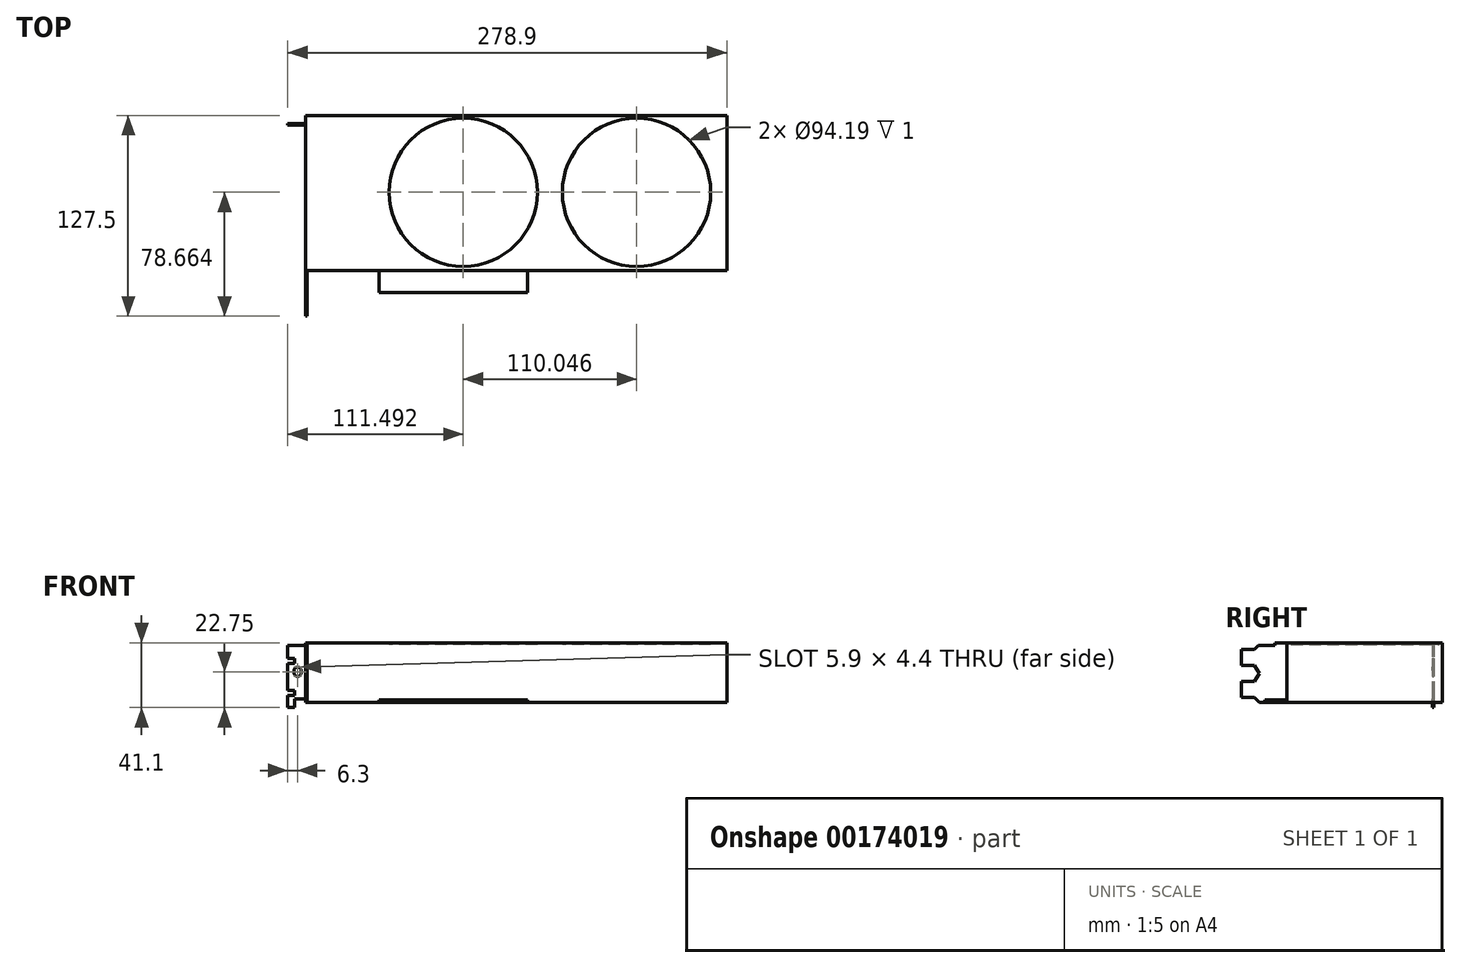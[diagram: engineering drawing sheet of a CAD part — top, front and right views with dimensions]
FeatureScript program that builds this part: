
annotation { "Feature Type Name" : "Feature", "Feature Type Description" : "" }
export const myFeature = defineFeature(function(context is Context, id is Id, definition is map)
    precondition{}
    {
        {
            var Q0;
            Q0=qCreatedBy(makeId("Top.planeOp"),FACE);
            var sketch = newSketch(context, id + "F0", { "sketchPlane" : qUnion([Q0])});
            skLineSegment(sketch, "E0.bottom", {"start": v(133.35, -49.25) * mm, "end": v(-133.35, -49.25) * mm});
            skLineSegment(sketch, "E0.top", {"start": v(133.35, 49.25) * mm, "end": v(-133.35, 49.25) * mm});
            skLineSegment(sketch, "E0.left", {"start": v(133.35, -49.25) * mm, "end": v(133.35, 49.25) * mm});
            skLineSegment(sketch, "E0.right", {"start": v(-133.35, -49.25) * mm, "end": v(-133.35, 49.25) * mm});
            skPoint(sketch, "E0.middle", {"position": v(0, 0) * mm});
            skSolve(sketch);
        }
        {
            var Q0;
            Q0 = qSketchRegion(id + "F0", true);
            extrude(context, id + "F1", {"entities" : qUnion([Q0]), "depth" : 38 * mm});
        }
        {
            var Q0;
            Q0=makeQuery(id+"F1.opExtrude","CAP_FACE",FACE,{"disambiguationData":[OSD([sQuery(id+"F0.wireOp",EDGE,"E0.bottom"),sQuery(id+"F0.wireOp",EDGE,"E0.top"),sQuery(id+"F0.wireOp",EDGE,"E0.left"),sQuery(id+"F0.wireOp",EDGE,"E0.right")])],"isStart":false});
            var sketch = newSketch(context, id + "F2", { "sketchPlane" : qUnion([Q0])});
            skCircle(sketch, "E1", {"center": v(-34.06, 0.41) * mm, "radius": 47.1 * mm});
            skCircle(sketch, "E2", {"center": v(75.99, 0.41) * mm, "radius": 47.1 * mm});
            skSolve(sketch);
        }
        {
            var Q0;
            Q0 = qSketchRegion(id + "F2", true);
            extrude(context, id + "F3", {"entities" : qUnion([Q0]), "operationType" : NewBodyOperationType.REMOVE, "oppositeDirection" : true, "depth" : 1 * mm});
        }
        {
            var Q0;
            Q0=makeQuery(id+"F1.opExtrude","SWEPT_FACE",FACE,{"disambiguationData":[OSD([sQuery(id+"F0.wireOp",EDGE,"E0.right")])]});
            var sketch = newSketch(context, id + "F4", { "sketchPlane" : qUnion([Q0])});
            skLineSegment(sketch, "E3.0", {"start": v(49.25, 38) * mm, "end": v(-49.25, 38) * mm});
            skLineSegment(sketch, "E3.1", {"start": v(-49.25, 38) * mm, "end": v(-49.25, 0) * mm});
            skLineSegment(sketch, "E3.2", {"start": v(49.25, 0) * mm, "end": v(-49.25, 0) * mm});
            skLineSegment(sketch, "E3.3", {"start": v(49.25, 38) * mm, "end": v(49.25, 0) * mm, "construction": true});
            skLineSegment(sketch, "E4", {"start": v(67.35, 36.4) * mm, "end": v(69.95, 33.8) * mm});
            skLineSegment(sketch, "E5", {"start": v(69.95, 33.8) * mm, "end": v(78.25, 33.8) * mm});
            skLineSegment(sketch, "E6", {"start": v(78.25, 33.8) * mm, "end": v(78.25, 23.5) * mm});
            skLineSegment(sketch, "E7", {"start": v(78.25, 23.5) * mm, "end": v(69.95, 23.5) * mm});
            skLineSegment(sketch, "E8", {"start": v(69.95, 23.5) * mm, "end": v(66.95, 18.5) * mm});
            skLineSegment(sketch, "E9", {"start": v(69.95, 13.5) * mm, "end": v(66.95, 18.5) * mm});
            skLineSegment(sketch, "E10", {"start": v(69.95, 13.5) * mm, "end": v(78.25, 13.5) * mm});
            skLineSegment(sketch, "E11", {"start": v(78.25, 13.5) * mm, "end": v(78.25, 3.2) * mm});
            skLineSegment(sketch, "E12", {"start": v(78.25, 3.2) * mm, "end": v(69.95, 3.2) * mm});
            skLineSegment(sketch, "E13", {"start": v(66.75, 0) * mm, "end": v(69.95, 3.2) * mm});
            skLineSegment(sketch, "E14", {"start": v(66.75, 0) * mm, "end": v(49.25, 0) * mm});
            skLineSegment(sketch, "E15", {"start": v(67.35, 36.4) * mm, "end": v(56.85, 36.4) * mm});
            skLineSegment(sketch, "E16", {"start": v(56.85, 36.4) * mm, "end": v(56.85, 38) * mm});
            skLineSegment(sketch, "E17", {"start": v(56.85, 38) * mm, "end": v(49.25, 38) * mm});
            skSolve(sketch);
        }
        {
            var Q0;
            Q0 = qSketchRegion(id + "F4", true);
            extrude(context, id + "F5", {"entities" : qUnion([Q0]), "operationType" : NewBodyOperationType.ADD, "depth" : .9 * mm});
        }
        {
            var Q0;
            Q0=makeQuery(id+"F5.opExtrude","CAP_FACE",FACE,{"disambiguationData":[OSD([sQuery(id+"F4.wireOp",EDGE,"E3.0"),sQuery(id+"F4.wireOp",EDGE,"E3.1"),sQuery(id+"F4.wireOp",EDGE,"E3.2"),sQuery(id+"F4.wireOp",EDGE,"E4"),sQuery(id+"F4.wireOp",EDGE,"E5"),sQuery(id+"F4.wireOp",EDGE,"E6"),sQuery(id+"F4.wireOp",EDGE,"E7"),sQuery(id+"F4.wireOp",EDGE,"E8"),sQuery(id+"F4.wireOp",EDGE,"E9"),sQuery(id+"F4.wireOp",EDGE,"E10"),sQuery(id+"F4.wireOp",EDGE,"E11"),sQuery(id+"F4.wireOp",EDGE,"E12"),sQuery(id+"F4.wireOp",EDGE,"E13"),sQuery(id+"F4.wireOp",EDGE,"E14"),sQuery(id+"F4.wireOp",EDGE,"E15"),sQuery(id+"F4.wireOp",EDGE,"E16"),sQuery(id+"F4.wireOp",EDGE,"E17")])],"isStart":false});
            var sketch = newSketch(context, id + "F6", { "sketchPlane" : qUnion([Q0])});
            skLineSegment(sketch, "E18.bottom", {"start": v(-44.05, 36.4) * mm, "end": v(-43.15, 36.4) * mm});
            skLineSegment(sketch, "E18.top", {"start": v(-44.05, -3.1) * mm, "end": v(-43.15, -3.1) * mm});
            skLineSegment(sketch, "E18.left", {"start": v(-44.05, 36.4) * mm, "end": v(-44.05, -3.1) * mm});
            skLineSegment(sketch, "E18.right", {"start": v(-43.15, 36.4) * mm, "end": v(-43.15, -3.1) * mm});
            skSolve(sketch);
        }
        {
            var Q0;
            Q0 = qSketchRegion(id + "F6", true);
            extrude(context, id + "F7", {"entities" : qUnion([Q0]), "operationType" : NewBodyOperationType.ADD, "depth" : 11.3 * mm});
        }
        {
            var Q0;
            Q0=makeQuery(id+"F7.opExtrude","SWEPT_FACE",FACE,{"disambiguationData":[OSD([sQuery(id+"F6.wireOp",EDGE,"E18.left")])]});
            var sketch = newSketch(context, id + "F8", { "sketchPlane" : qUnion([Q0])});
            skLineSegment(sketch, "E19.bottom", {"start": v(134.25, -3.1) * mm, "end": v(141.25, -3.1) * mm});
            skLineSegment(sketch, "E19.top", {"start": v(134.25, 2.3) * mm, "end": v(141.25, 2.3) * mm});
            skLineSegment(sketch, "E19.left", {"start": v(134.25, -3.1) * mm, "end": v(134.25, 2.3) * mm});
            skLineSegment(sketch, "E19.right", {"start": v(141.25, -3.1) * mm, "end": v(141.25, 2.3) * mm});
            skLineSegment(sketch, "E20.bottom", {"start": v(145.55, 28) * mm, "end": v(141.25, 28) * mm});
            skLineSegment(sketch, "E20.top", {"start": v(145.55, 25) * mm, "end": v(141.25, 25) * mm});
            skLineSegment(sketch, "E20.left", {"start": v(145.55, 28) * mm, "end": v(145.55, 25) * mm});
            skLineSegment(sketch, "E20.right", {"start": v(141.25, 28) * mm, "end": v(141.25, 25) * mm});
            skLineSegment(sketch, "E21.bottom", {"start": v(145.55, 7.7) * mm, "end": v(141.25, 7.7) * mm});
            skLineSegment(sketch, "E21.top", {"start": v(145.55, 4.7) * mm, "end": v(141.25, 4.7) * mm});
            skLineSegment(sketch, "E21.left", {"start": v(145.55, 7.7) * mm, "end": v(145.55, 4.7) * mm});
            skLineSegment(sketch, "E21.right", {"start": v(141.25, 7.7) * mm, "end": v(141.25, 4.7) * mm});
            skLineSegment(sketch, "E22", {"start": v(139.25, 20.4) * mm, "end": v(139.25, 18.9) * mm, "construction": true});
            skArc(sketch, "E23.0.startCap", {"start": v(137.05, 20.4) * mm, "mid": v(139.25, 22.6) * mm, "end": v(141.45, 20.4) * mm});
            skArc(sketch, "E23.0.endCap", {"start": v(141.45, 18.9) * mm, "mid": v(139.25, 16.7) * mm, "end": v(137.05, 18.9) * mm});
            skLineSegment(sketch, "E23.0.left", {"start": v(141.45, 20.4) * mm, "end": v(141.45, 18.9) * mm});
            skLineSegment(sketch, "E23.0.right", {"start": v(137.05, 20.4) * mm, "end": v(137.05, 18.9) * mm});
            skSolve(sketch);
        }
        {
            var Q0;
            Q0 = qSketchRegion(id + "F8", true);
            extrude(context, id + "F9", {"entities" : qUnion([Q0]), "operationType" : NewBodyOperationType.REMOVE, "endBound" : BoundingType.UP_TO_NEXT, "oppositeDirection" : true, "depth" : 25 * mm});
        }
        {
            var Q0;
            Q0=makeQuery(id+"F1.opExtrude","SWEPT_FACE",FACE,{"disambiguationData":[OSD([sQuery(id+"F0.wireOp",EDGE,"E0.bottom")])]});
            var sketch = newSketch(context, id + "F10", { "sketchPlane" : qUnion([Q0])});
            skLineSegment(sketch, "E24.bottom", {"start": v(-87.35, 0) * mm, "end": v(6.65, 0) * mm});
            skLineSegment(sketch, "E24.top", {"start": v(-87.35, 1.6) * mm, "end": v(6.65, 1.6) * mm});
            skLineSegment(sketch, "E24.left", {"start": v(-87.35, 0) * mm, "end": v(-87.35, 1.6) * mm});
            skLineSegment(sketch, "E24.right", {"start": v(6.65, 0) * mm, "end": v(6.65, 1.6) * mm});
            skSolve(sketch);
        }
        {
            var Q0;
            Q0 = qSketchRegion(id + "F10", true);
            extrude(context, id + "F11", {"entities" : qUnion([Q0]), "operationType" : NewBodyOperationType.ADD, "depth" : 14 * mm});
        }
    });
